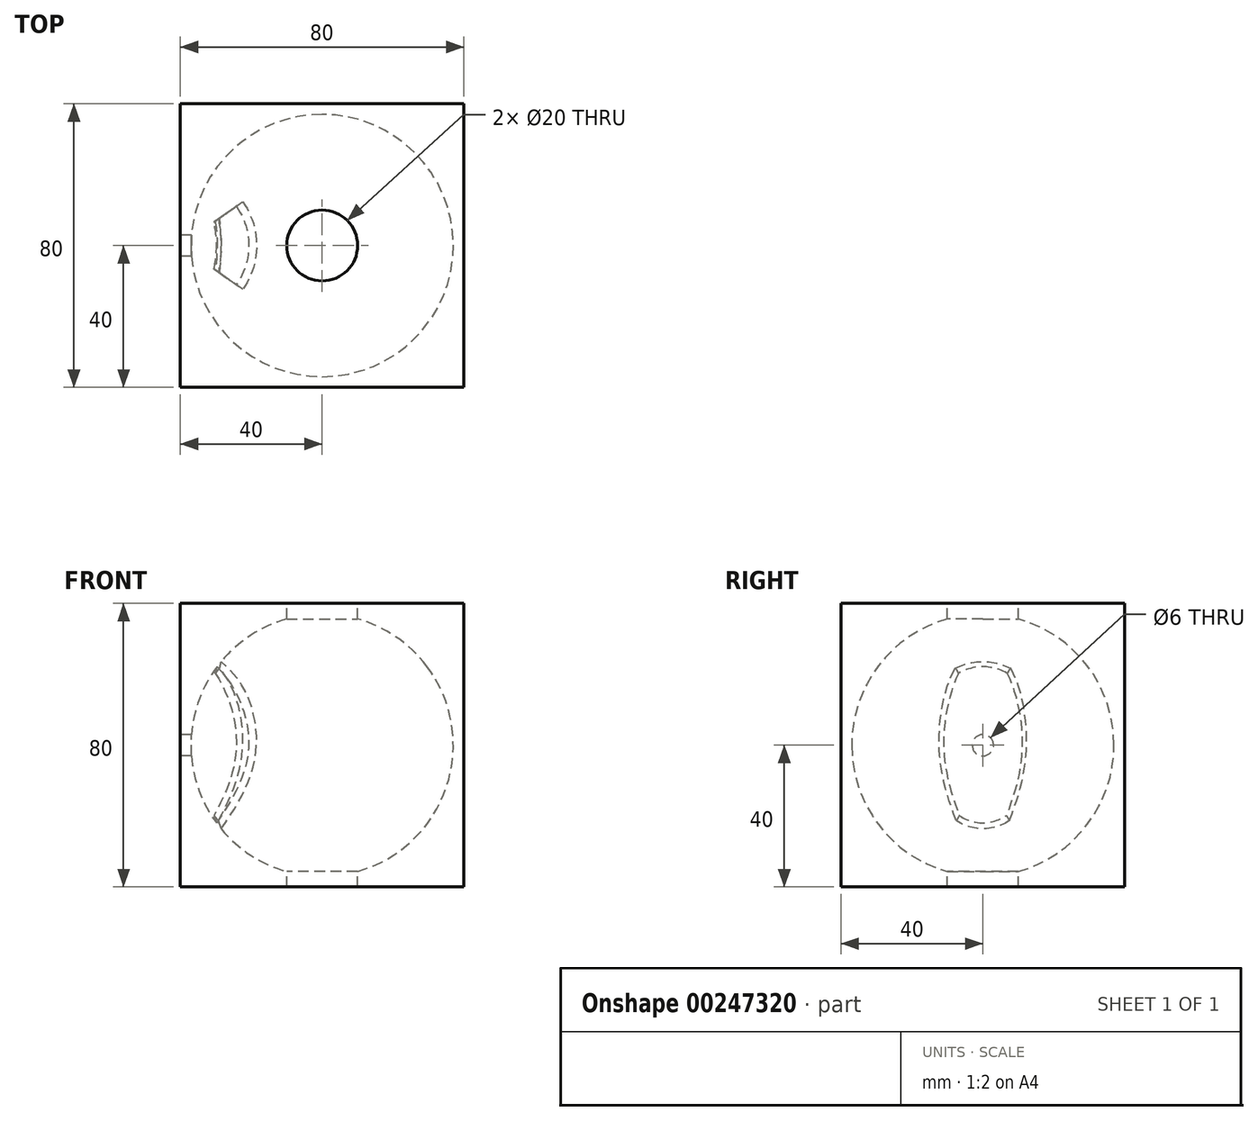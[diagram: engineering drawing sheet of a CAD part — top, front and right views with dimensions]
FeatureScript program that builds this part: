
annotation { "Feature Type Name" : "Feature", "Feature Type Description" : "" }
export const myFeature = defineFeature(function(context is Context, id is Id, definition is map)
    precondition{}
    {
        {
            var Q0;
            Q0=qCreatedBy(makeId("Top.planeOp"),FACE);
            var sketch = newSketch(context, id + "F0", { "sketchPlane" : qUnion([Q0])});
            skArc(sketch, "E0", {"start": v(0, -37) * mm, "mid": v(37, 0) * mm, "end": v(0, 37) * mm});
            skLineSegment(sketch, "E1", {"start": v(0, 38.44) * mm, "end": v(0, -38.44) * mm});
            skSolve(sketch);
        }
        {
            var Q0;
            {var subQ0=sQuery(id+"F0.wireOp",EDGE,"DYxJ9GRZ-q8qz-Q0Qq-K3Mr-sF3iiEksJAOO");Q0=makeQuery(id+"F0.imprint","IMPRINT",FACE,{"disambiguationData":[TD([[makeQuery(id+"F0.imprint","IMPRINT",EDGE,{"derivedFrom":subQ0}),1.0]])]});}
            var Q1;
            {var subQ0=sQuery(id+"F0.wireOp",EDGE,"E0");Q1=makeQuery(id+"F0.imprint","IMPRINT",FACE,{"disambiguationData":[TD([[makeQuery(id+"F0.imprint","IMPRINT",EDGE,{"derivedFrom":subQ0}),1.0]])]});}
            var Q2;
            Q2=sQuery(id+"F0.wireOp",EDGE,"E1");
            revolve(context, id + "F1", {"entities" : qUnion([Q0, Q1]), "axis" : qUnion([Q2]), "revolveType" : RevolveType.FULL});
        }
        {
            var Q0;
            Q0=qCreatedBy(makeId("Top.planeOp"),FACE);
            var sketch = newSketch(context, id + "F2", { "sketchPlane" : qUnion([Q0])});
            skLineSegment(sketch, "E2.bottom", {"start": v(40, 40) * mm, "end": v(-40, 40) * mm});
            skLineSegment(sketch, "E2.top", {"start": v(40, -40) * mm, "end": v(-40, -40) * mm});
            skLineSegment(sketch, "E2.left", {"start": v(40, 40) * mm, "end": v(40, -40) * mm});
            skLineSegment(sketch, "E2.right", {"start": v(-40, 40) * mm, "end": v(-40, -40) * mm});
            skPoint(sketch, "E2.middle", {"position": v(0, 0) * mm});
            skSolve(sketch);
        }
        {
            var Q0;
            Q0=makeQuery(id+"F2.imprint","IMPRINT",FACE,{"disambiguationData":[TD([[makeQuery(id+"F2.imprint","IMPRINT",EDGE,{"derivedFrom":sQuery(id+"F2.wireOp",EDGE,"E2.bottom")}),1.0]])]});
            extrude(context, id + "F3", {"entities" : qUnion([Q0]), "endBound" : BoundingType.SYMMETRIC, "depth" : 80 * mm});
        }
        {
            var Q0;
            Q0=makeQuery(id+"F1.opRevolve","SWEPT_BODY",BODY,{"disambiguationData":[OSD([sQuery(id+"F0.wireOp",EDGE,"E0"),sQuery(id+"F0.wireOp",EDGE,"E1")])]});
            var Q1;
            Q1=makeQuery(id+"F3.opExtrude","SWEPT_BODY",BODY,{"disambiguationData":[OSD([sQuery(id+"F2.wireOp",EDGE,"E2.bottom"),sQuery(id+"F2.wireOp",EDGE,"E2.top"),sQuery(id+"F2.wireOp",EDGE,"E2.left"),sQuery(id+"F2.wireOp",EDGE,"E2.right")])]});
            booleanBodies(context, id + "F4", {"operationType" : BooleanOperationType.SUBTRACTION, "tools" : qUnion([Q0]), "targets" : qUnion([Q1])});
        }
        {
            var Q0;
            Q0=qCreatedBy(makeId("Front.planeOp"),FACE);
            var sketch = newSketch(context, id + "F5", { "sketchPlane" : qUnion([Q0])});
            skPoint(sketch, "E3.0", {"position": v(-40, 40) * mm});
            skPoint(sketch, "E4.0", {"position": v(-40, -40) * mm});
            skLineSegment(sketch, "E5", {"start": v(-40, 40) * mm, "end": v(-40, -40) * mm});
            skSolve(sketch);
        }
        {
            var Q0;
            Q0=qCreatedBy(makeId("Front.planeOp"),FACE);
            var sketch = newSketch(context, id + "F6", { "sketchPlane" : qUnion([Q0])});
            skCircle(sketch, "E6", {"center": v(0, 0) * mm, "radius": 37 * mm});
            skFitSpline(sketch, "E7", {"points": [v(-28.5, -23.6) * mm, v(-18.54, 0) * mm, v(-28.5, 23.6) * mm], "startDerivative": vector(35.3, 50.23) * mm, "endDerivative": vector(-44.54, 35.2) * mm});
            skLineSegment(sketch, "E8", {"start": v(-28.5, -23.6) * mm, "end": v(-28.5, 23.6) * mm, "construction": true});
            skFitSpline(sketch, "E9", {"points": [v(-29.64, 22.15) * mm, v(-20.72, 0) * mm, v(-29.81, -21.91) * mm], "startDerivative": vector(35.6, -37) * mm, "endDerivative": vector(-31.6, -45.67) * mm});
            skArc(sketch, "E10", {"start": v(-29.81, -21.91) * mm, "mid": v(-29.17, -22.77) * mm, "end": v(-28.5, -23.6) * mm});
            skArc(sketch, "E11", {"start": v(-28.5, 23.6) * mm, "mid": v(-29.08, 22.88) * mm, "end": v(-29.64, 22.15) * mm});
            skSolve(sketch);
        }
        {
            var Q0;
            {var subQ0=sQuery(id+"F6.wireOp",EDGE,"E7");Q0=makeQuery(id+"F6.imprint","IMPRINT",FACE,{"disambiguationData":[TD([[makeQuery(id+"F6.imprint","IMPRINT",EDGE,{"derivedFrom":subQ0}),1.0]])]});}
            var Q1;
            Q1=sQuery(id+"F5.wireOp",EDGE,"E5");
            revolve(context, id + "F7", {"operationType" : NewBodyOperationType.ADD, "entities" : qUnion([Q0]), "axis" : qUnion([Q1]), "revolveType" : RevolveType.SYMMETRIC, "angle" : 70 * degree});
        }
        {
            var Q0;
            Q0=makeQuery(id+"F3.opExtrude","SWEPT_FACE",FACE,{"disambiguationData":[OSD([sQuery(id+"F2.wireOp",EDGE,"E2.right")])]});
            var sketch = newSketch(context, id + "F8", { "sketchPlane" : qUnion([Q0])});
            skCircle(sketch, "E12", {"center": v(0, 0) * mm, "radius": 3 * mm});
            skSolve(sketch);
        }
        {
            var Q0;
            Q0=makeQuery(id+"F8.imprint","IMPRINT",FACE,{"disambiguationData":[TD([[makeQuery(id+"F8.imprint","IMPRINT",EDGE,{"derivedFrom":sQuery(id+"F8.wireOp",EDGE,"E12")}),1.0]])]});
            extrude(context, id + "F9", {"entities" : qUnion([Q0]), "operationType" : NewBodyOperationType.REMOVE, "endBound" : BoundingType.SYMMETRIC, "oppositeDirection" : true, "depth" : 8 * mm});
        }
        {
            var Q0;
            Q0=makeQuery(id+"F3.opExtrude","CAP_FACE",FACE,{"disambiguationData":[OSD([sQuery(id+"F2.wireOp",EDGE,"E2.bottom"),sQuery(id+"F2.wireOp",EDGE,"E2.top"),sQuery(id+"F2.wireOp",EDGE,"E2.left"),sQuery(id+"F2.wireOp",EDGE,"E2.right")])],"isStart":false});
            var sketch = newSketch(context, id + "F10", { "sketchPlane" : qUnion([Q0])});
            skCircle(sketch, "E13", {"center": v(0, 0) * mm, "radius": 10 * mm});
            skSolve(sketch);
        }
        {
            var Q0;
            Q0=makeQuery(id+"F10.imprint","IMPRINT",FACE,{"disambiguationData":[TD([[makeQuery(id+"F10.imprint","IMPRINT",EDGE,{"derivedFrom":sQuery(id+"F10.wireOp",EDGE,"E13")}),1.0]])]});
            extrude(context, id + "F11", {"entities" : qUnion([Q0]), "operationType" : NewBodyOperationType.REMOVE, "endBound" : BoundingType.SYMMETRIC, "oppositeDirection" : true, "depth" : 10 * mm});
        }
        {
            var Q0;
            Q0=makeQuery(id+"F3.opExtrude","CAP_FACE",FACE,{"disambiguationData":[OSD([sQuery(id+"F2.wireOp",EDGE,"E2.bottom"),sQuery(id+"F2.wireOp",EDGE,"E2.top"),sQuery(id+"F2.wireOp",EDGE,"E2.left"),sQuery(id+"F2.wireOp",EDGE,"E2.right")])],"isStart":true});
            var sketch = newSketch(context, id + "F12", { "sketchPlane" : qUnion([Q0])});
            skCircle(sketch, "E14.0", {"center": v(0, 0) * mm, "radius": 10 * mm});
            skSolve(sketch);
        }
        {
            var Q0;
            Q0=makeQuery(id+"F12.imprint","IMPRINT",FACE,{"disambiguationData":[TD([[makeQuery(id+"F12.imprint","IMPRINT",EDGE,{"derivedFrom":sQuery(id+"F12.wireOp",EDGE,"E14.0")}),1.0]])]});
            extrude(context, id + "F13", {"entities" : qUnion([Q0]), "operationType" : NewBodyOperationType.REMOVE, "endBound" : BoundingType.SYMMETRIC, "depth" : 10 * mm});
        }
    });
